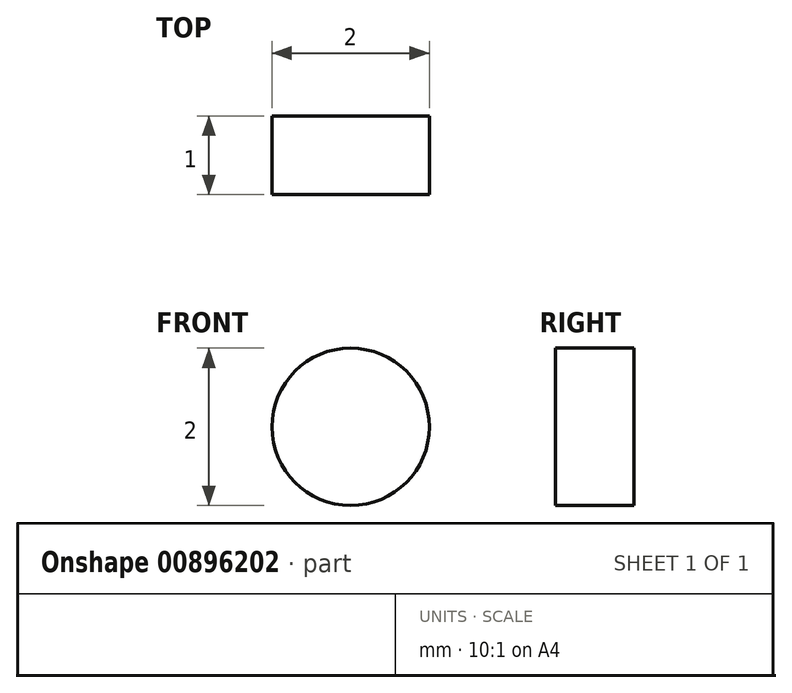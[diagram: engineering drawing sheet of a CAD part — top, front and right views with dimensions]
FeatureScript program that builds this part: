
annotation { "Feature Type Name" : "Feature", "Feature Type Description" : "" }
export const myFeature = defineFeature(function(context is Context, id is Id, definition is map)
    precondition{}
    {
        {
            var Q0;
            Q0=qCreatedBy(makeId("Front.planeOp"),FACE);
            var sketch = newSketch(context, id + "F0", { "sketchPlane" : qUnion([Q0])});
            skCircle(sketch, "E0", {"center": v(0, 0) * mm, "radius": 1 * mm});
            skSolve(sketch);
        }
        {
            var Q0;
            Q0 = qSketchRegion(id + "F0", true);
            extrude(context, id + "F1", {"entities" : qUnion([Q0]), "depth" : 1 * mm, "offsetDistance" : 25 * mm});
        }
    });
